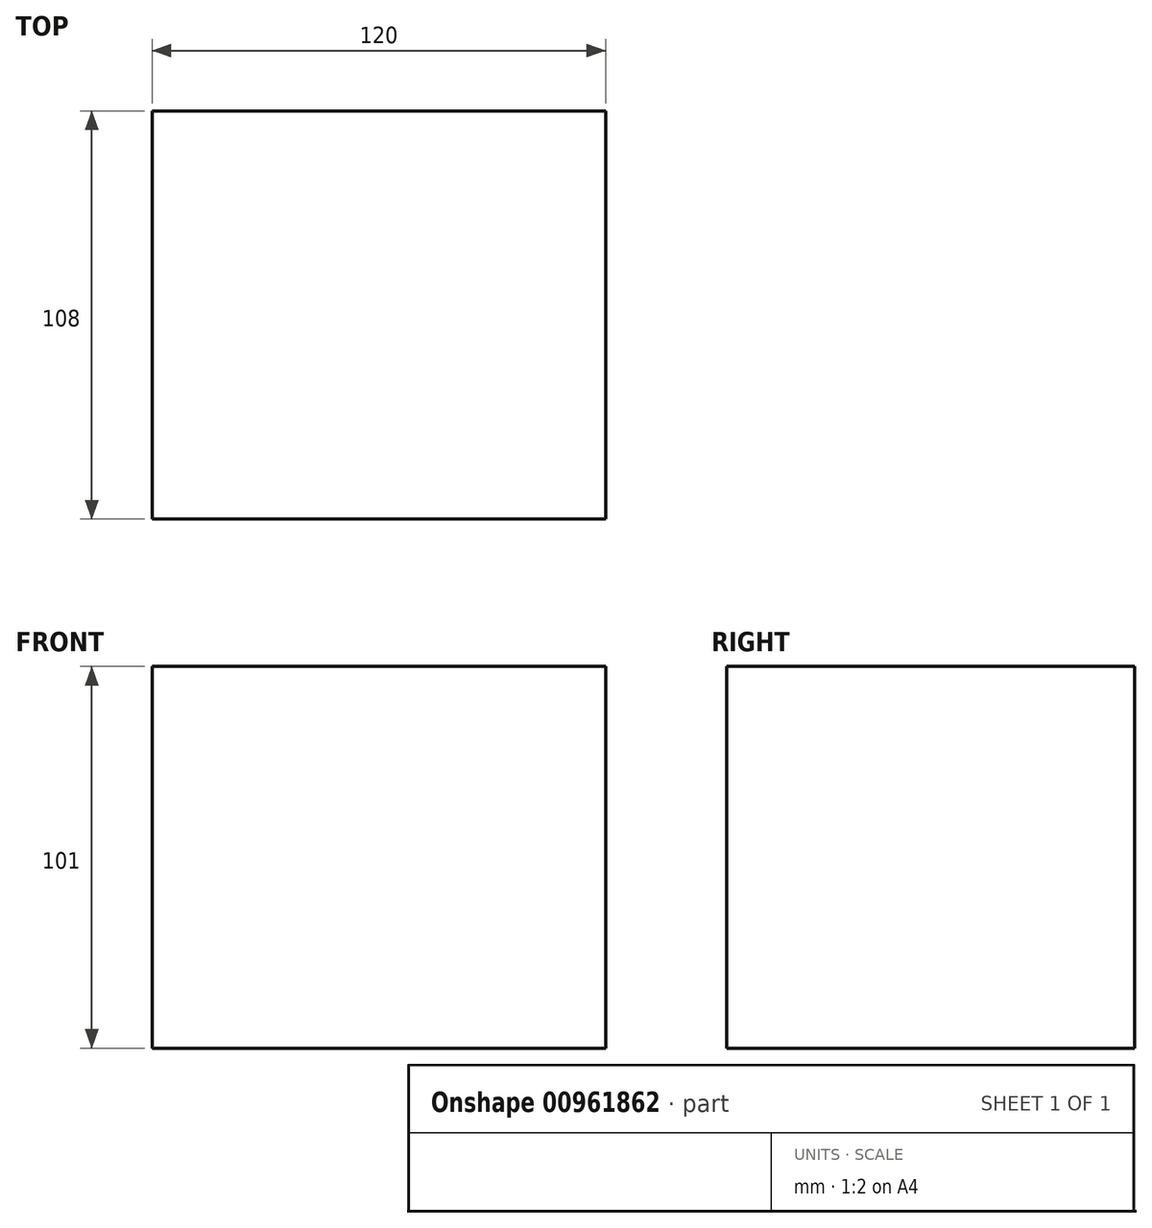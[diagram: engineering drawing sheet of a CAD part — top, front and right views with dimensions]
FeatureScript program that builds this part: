
annotation { "Feature Type Name" : "Feature", "Feature Type Description" : "" }
export const myFeature = defineFeature(function(context is Context, id is Id, definition is map)
    precondition{}
    {
        {
            var Q0;
            Q0=qCreatedBy(makeId("Top.planeOp"),FACE);
            var sketch = newSketch(context, id + "F0", { "sketchPlane" : qUnion([Q0])});
            skLineSegment(sketch, "E0.bottom", {"start": v(-34.07, 63.87) * mm, "end": v(85.93, 63.87) * mm});
            skLineSegment(sketch, "E0.top", {"start": v(-34.07, -44.13) * mm, "end": v(85.93, -44.13) * mm});
            skLineSegment(sketch, "E0.left", {"start": v(-34.07, 63.87) * mm, "end": v(-34.07, -44.13) * mm});
            skLineSegment(sketch, "E0.right", {"start": v(85.93, 63.87) * mm, "end": v(85.93, -44.13) * mm});
            skSolve(sketch);
        }
        {
            var Q0;
            Q0 = qSketchRegion(id + "F0", true);
            extrude(context, id + "F1", {"entities" : qUnion([Q0]), "depth" : 101 * mm, "offsetDistance" : 25 * mm});
        }
    });
